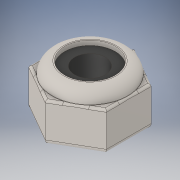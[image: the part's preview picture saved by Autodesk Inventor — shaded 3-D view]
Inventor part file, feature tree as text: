
AUTODESK INVENTOR PART (.ipt)
format: ipt  version: 2017 (Build 210142000, 142)  size: 203,264 bytes
history: native  units: in
note: dims shown in document units (in); Inventor stores cm internally (conversion verified against a paired STEP export)
features: fillet x1
ambient origin geometry x8: Origin, YZ Plane, XZ Plane, XY Plane, X Axis, Y Axis, Z Axis, Center Point
bodies: Solid1 (feature_tree)
feature tree (1):
  fillet  "Fillet6"  [1 undecoded]
note: 1 required parameter value undecoded (feature->parameter linkage not recoverable at this tier; creation-order binding heuristic only, values carry confidence <= 0.55)
